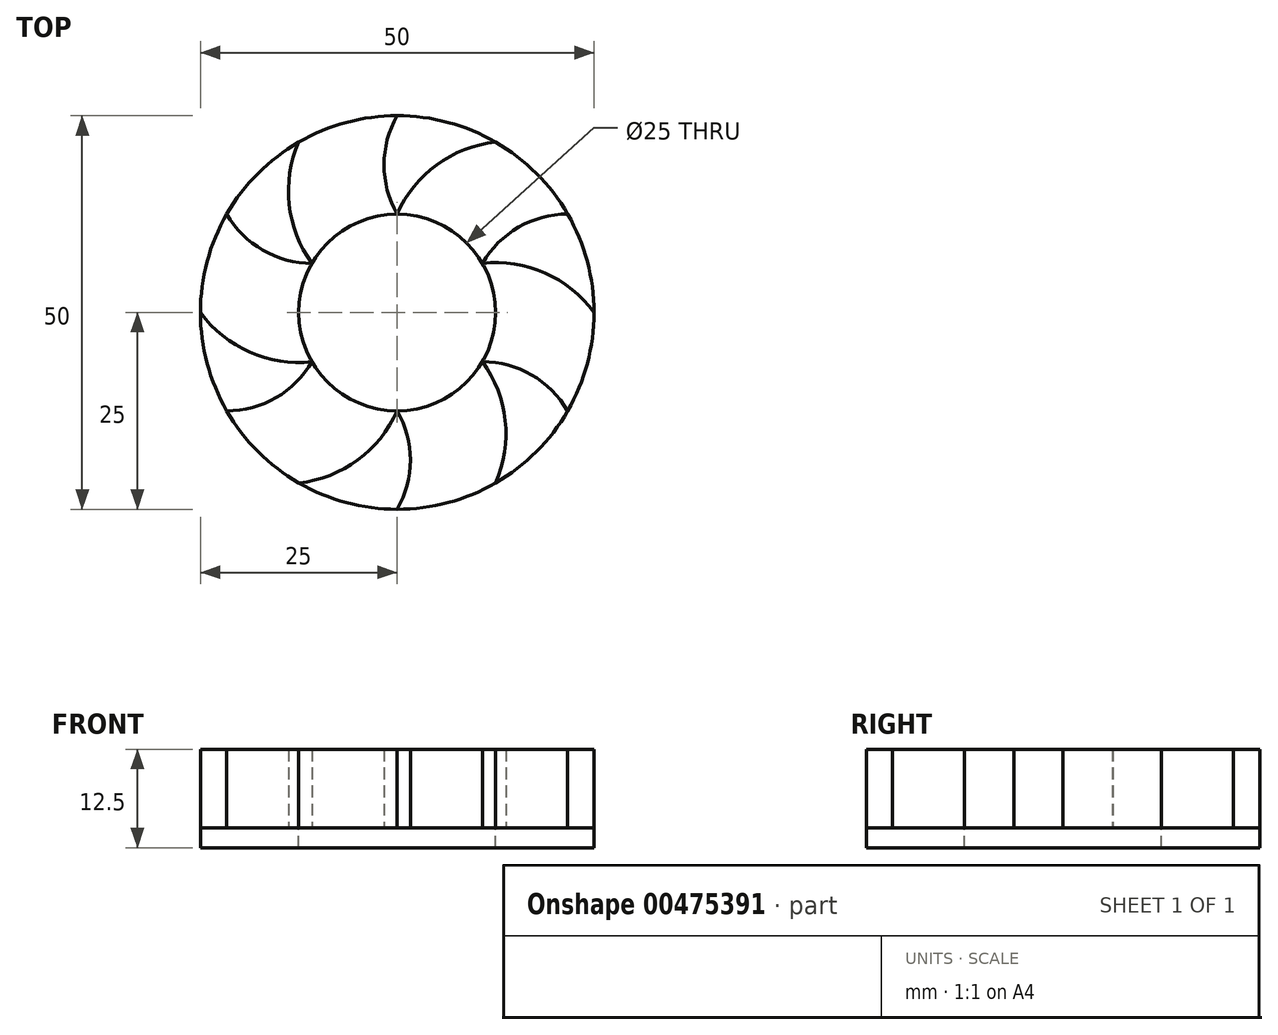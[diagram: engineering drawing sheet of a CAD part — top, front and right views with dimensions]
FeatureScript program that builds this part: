
annotation { "Feature Type Name" : "Feature", "Feature Type Description" : "" }
export const myFeature = defineFeature(function(context is Context, id is Id, definition is map)
    precondition{}
    {
        {
            var Q0;
            Q0=qCreatedBy(makeId("Top.planeOp"),FACE);
            var sketch = newSketch(context, id + "F0", { "sketchPlane" : qUnion([Q0])});
            skCircle(sketch, "E0", {"center": v(0, 0) * mm, "radius": 25 * mm});
            skCircle(sketch, "E1", {"center": v(0, 0) * mm, "radius": 12.5 * mm});
            skLineSegment(sketch, "E2", {"start": v(0, 0) * mm, "end": v(21.65, 12.5) * mm, "construction": true});
            skLineSegment(sketch, "E3", {"start": v(0, 0) * mm, "end": v(12.5, 21.65) * mm});
            skLineSegment(sketch, "E4", {"start": v(0, 0) * mm, "end": v(-12.5, -21.65) * mm});
            skLineSegment(sketch, "E5", {"start": v(0, 0) * mm, "end": v(-21.65, -12.5) * mm, "construction": true});
            skLineSegment(sketch, "E6", {"start": v(-12.5, 21.65) * mm, "end": v(12.5, -21.65) * mm});
            skLineSegment(sketch, "E7", {"start": v(0, 0) * mm, "end": v(-21.65, 12.5) * mm, "construction": true});
            skLineSegment(sketch, "E8", {"start": v(0, 0) * mm, "end": v(21.65, -12.5) * mm, "construction": true});
            skPoint(sketch, "E9", {"position": v(6.25, 10.83) * mm});
            skPoint(sketch, "E10", {"position": v(10.83, 6.25) * mm});
            skPoint(sketch, "E11", {"position": v(10.83, -6.25) * mm});
            skPoint(sketch, "E12", {"position": v(6.25, -10.83) * mm});
            skPoint(sketch, "E13", {"position": v(-6.25, -10.83) * mm});
            skPoint(sketch, "E14", {"position": v(-10.83, -6.25) * mm});
            skPoint(sketch, "E15", {"position": v(-10.83, 6.25) * mm});
            skPoint(sketch, "E16", {"position": v(-6.25, 10.83) * mm});
            skLineSegment(sketch, "E17", {"start": v(25, 0) * mm, "end": v(-25, 0) * mm});
            skLineSegment(sketch, "E18", {"start": v(0, 25) * mm, "end": v(0, -25) * mm, "construction": true});
            skArc(sketch, "E19", {"start": v(25, 0) * mm, "mid": v(12.5, 6.34) * mm, "end": v(0, 0) * mm});
            skPoint(sketch, "E20", {"position": v(0, 12.5) * mm});
            skPoint(sketch, "E21", {"position": v(-12.5, 0) * mm});
            skPoint(sketch, "E22", {"position": v(12.5, 0) * mm});
            skPoint(sketch, "E23", {"position": v(0, -12.5) * mm});
            skArc(sketch, "E24", {"start": v(12.5, 21.65) * mm, "mid": v(0.76, 14) * mm, "end": v(0, 0) * mm});
            skArc(sketch, "E25", {"start": v(-12.5, 21.65) * mm, "mid": v(-11.74, 7.65) * mm, "end": v(0, 0) * mm});
            skArc(sketch, "E26", {"start": v(-25, 0) * mm, "mid": v(-12.5, -6.34) * mm, "end": v(0, 0) * mm});
            skArc(sketch, "E27", {"start": v(-12.5, -21.65) * mm, "mid": v(-0.76, -14) * mm, "end": v(0, 0) * mm});
            skArc(sketch, "E28", {"start": v(12.5, -21.65) * mm, "mid": v(11.74, -7.65) * mm, "end": v(0, 0) * mm});
            skArc(sketch, "E29", {"start": v(21.65, 12.5) * mm, "mid": v(7.65, 11.74) * mm, "end": v(0, 0) * mm});
            skArc(sketch, "E30", {"start": v(0, 25) * mm, "mid": v(-6.34, 12.5) * mm, "end": v(0, 0) * mm});
            skArc(sketch, "E31", {"start": v(-21.65, 12.5) * mm, "mid": v(-14, 0.76) * mm, "end": v(0, 0) * mm});
            skArc(sketch, "E32", {"start": v(-21.65, -12.5) * mm, "mid": v(-7.65, -11.74) * mm, "end": v(0, 0) * mm});
            skArc(sketch, "E33", {"start": v(0, -25) * mm, "mid": v(6.34, -12.5) * mm, "end": v(0, 0) * mm});
            skArc(sketch, "E34", {"start": v(21.65, -12.5) * mm, "mid": v(14, -0.76) * mm, "end": v(0, 0) * mm});
            skArc(sketch, "E35", {"start": v(21.65, 12.5) * mm, "mid": v(10.83, 6.25) * mm, "end": v(10.83, -6.25) * mm});
            skArc(sketch, "E36", {"start": v(0, 25) * mm, "mid": v(0, 12.5) * mm, "end": v(10.83, 6.25) * mm});
            skArc(sketch, "E37", {"start": v(-21.65, 12.5) * mm, "mid": v(-10.83, 6.25) * mm, "end": v(0, 12.5) * mm});
            skArc(sketch, "E38", {"start": v(-21.65, -12.5) * mm, "mid": v(-10.83, -6.25) * mm, "end": v(-10.83, 6.25) * mm});
            skArc(sketch, "E39", {"start": v(0, -25) * mm, "mid": v(0, -12.5) * mm, "end": v(-10.83, -6.25) * mm});
            skArc(sketch, "E40", {"start": v(21.65, -12.5) * mm, "mid": v(10.83, -6.25) * mm, "end": v(0, -12.5) * mm});
            skSolve(sketch);
        }
        {
            var Q0;
            {var subQ0=sQuery(id+"F0.wireOp",EDGE,"E19");var subQ1=sQuery(id+"F0.wireOp",EDGE,"E0");var subQ2=makeQuery(id+"F0.imprint","INTERSECT",VERTEX,{"derivedFrom":[subQ1,sQuery(id+"F0.wireOp",EDGE,"E17"),subQ0]});Q0=makeQuery(id+"F0.imprint","IMPRINT",FACE,{"disambiguationData":[TD([[makeQuery(id+"F0.imprint","IMPRINT",EDGE,{"disambiguationData":[TD([[subQ2,-1.0]])],"derivedFrom":subQ1}),1.0]])]});}
            var Q1;
            {var subQ0=sQuery(id+"F0.wireOp",EDGE,"E24");var subQ1=sQuery(id+"F0.wireOp",EDGE,"E0");var subQ2=makeQuery(id+"F0.imprint","INTERSECT",VERTEX,{"derivedFrom":[subQ1,sQuery(id+"F0.wireOp",EDGE,"E3"),subQ0]});Q1=makeQuery(id+"F0.imprint","IMPRINT",FACE,{"disambiguationData":[TD([[makeQuery(id+"F0.imprint","IMPRINT",EDGE,{"disambiguationData":[TD([[subQ2,-1.0]])],"derivedFrom":subQ1}),1.0]])]});}
            var Q2;
            {var subQ0=sQuery(id+"F0.wireOp",EDGE,"E25");var subQ1=sQuery(id+"F0.wireOp",EDGE,"E0");var subQ2=makeQuery(id+"F0.imprint","INTERSECT",VERTEX,{"derivedFrom":[subQ1,sQuery(id+"F0.wireOp",EDGE,"E6"),subQ0]});Q2=makeQuery(id+"F0.imprint","IMPRINT",FACE,{"disambiguationData":[TD([[makeQuery(id+"F0.imprint","IMPRINT",EDGE,{"disambiguationData":[TD([[subQ2,-1.0]])],"derivedFrom":subQ1}),1.0]])]});}
            var Q3;
            {var subQ0=sQuery(id+"F0.wireOp",EDGE,"E26");var subQ1=sQuery(id+"F0.wireOp",EDGE,"E0");var subQ2=makeQuery(id+"F0.imprint","INTERSECT",VERTEX,{"derivedFrom":[subQ1,sQuery(id+"F0.wireOp",EDGE,"E17"),subQ0]});Q3=makeQuery(id+"F0.imprint","IMPRINT",FACE,{"disambiguationData":[TD([[makeQuery(id+"F0.imprint","IMPRINT",EDGE,{"disambiguationData":[TD([[subQ2,-1.0]])],"derivedFrom":subQ1}),1.0]])]});}
            var Q4;
            {var subQ0=sQuery(id+"F0.wireOp",EDGE,"E27");var subQ1=sQuery(id+"F0.wireOp",EDGE,"E0");var subQ2=makeQuery(id+"F0.imprint","INTERSECT",VERTEX,{"derivedFrom":[subQ1,sQuery(id+"F0.wireOp",EDGE,"E4"),subQ0]});Q4=makeQuery(id+"F0.imprint","IMPRINT",FACE,{"disambiguationData":[TD([[makeQuery(id+"F0.imprint","IMPRINT",EDGE,{"disambiguationData":[TD([[subQ2,-1.0]])],"derivedFrom":subQ1}),1.0]])]});}
            var Q5;
            {var subQ0=sQuery(id+"F0.wireOp",EDGE,"E28");var subQ1=sQuery(id+"F0.wireOp",EDGE,"E0");var subQ2=makeQuery(id+"F0.imprint","INTERSECT",VERTEX,{"derivedFrom":[subQ1,sQuery(id+"F0.wireOp",EDGE,"E6"),subQ0]});Q5=makeQuery(id+"F0.imprint","IMPRINT",FACE,{"disambiguationData":[TD([[makeQuery(id+"F0.imprint","IMPRINT",EDGE,{"disambiguationData":[TD([[subQ2,-1.0]])],"derivedFrom":subQ1}),1.0]])]});}
            extrude(context, id + "F1", {"entities" : qUnion([Q0, Q1, Q2, Q3, Q4, Q5]), "depth" : 10 * mm});
        }
        {
            var Q0;
            Q0 = qSketchRegion(id + "F0", true);
            extrude(context, id + "F2", {"entities" : qUnion([Q0]), "oppositeDirection" : true, "depth" : 2.5 * mm, "offsetDistance" : 25 * mm});
        }
    });
